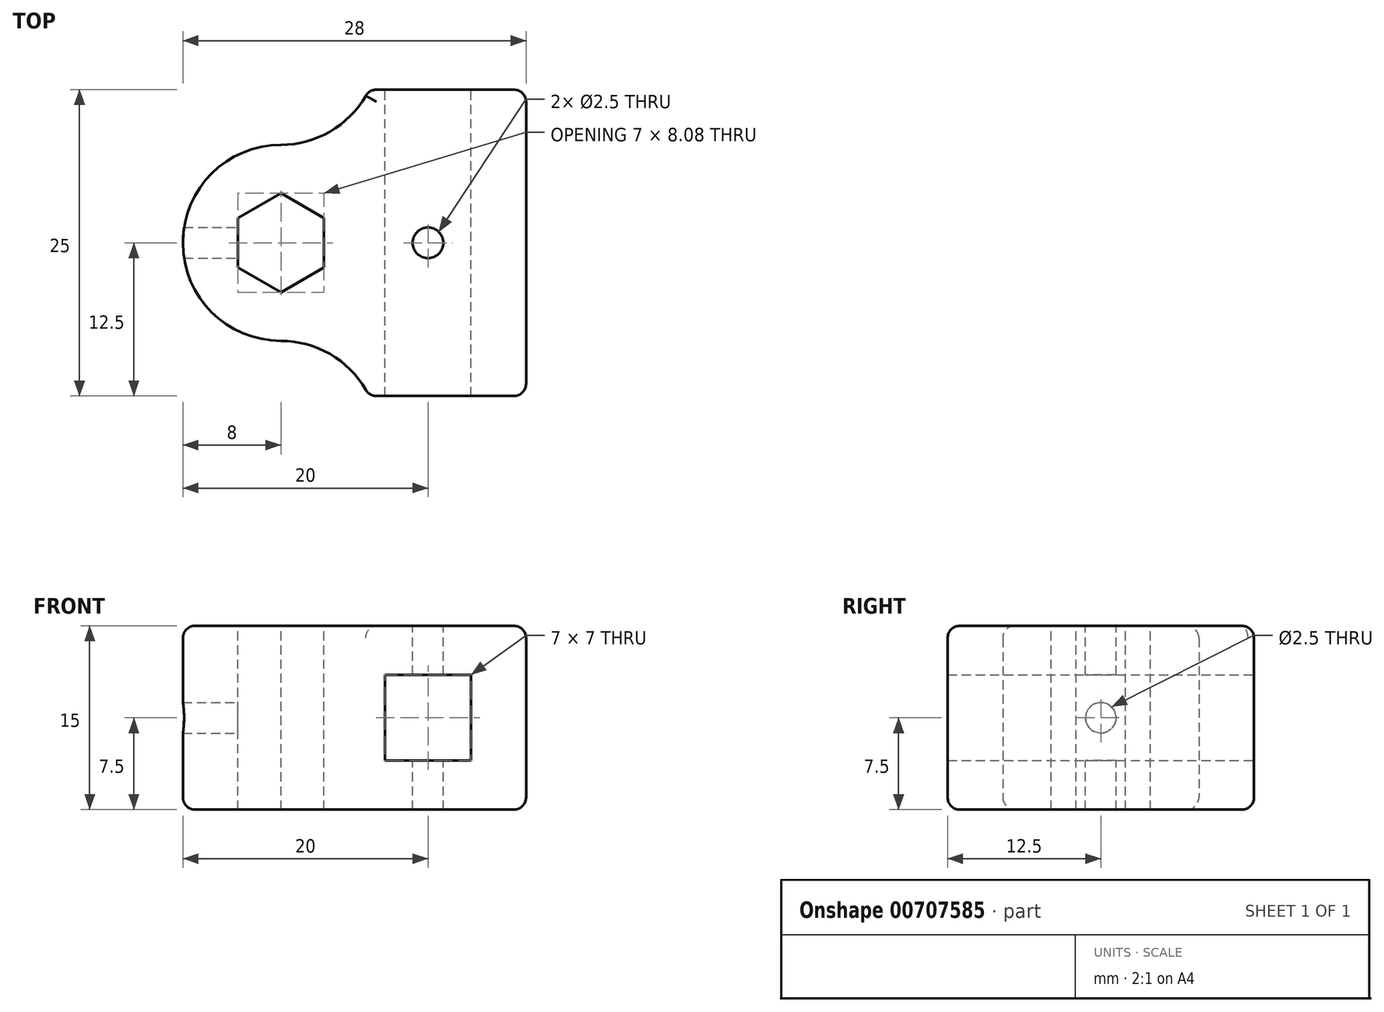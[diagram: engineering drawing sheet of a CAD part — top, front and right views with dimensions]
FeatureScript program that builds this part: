
annotation { "Feature Type Name" : "Feature", "Feature Type Description" : "" }
export const myFeature = defineFeature(function(context is Context, id is Id, definition is map)
    precondition{}
    {
        {
            var Q0;
            Q0=qCreatedBy(makeId("Front.planeOp"),FACE);
            var sketch = newSketch(context, id + "F0", { "sketchPlane" : qUnion([Q0])});
            skLineSegment(sketch, "E0.bottom", {"start": v(-3.5, -3.5) * mm, "end": v(3.5, -3.5) * mm});
            skLineSegment(sketch, "E0.top", {"start": v(-3.5, 3.5) * mm, "end": v(3.5, 3.5) * mm});
            skLineSegment(sketch, "E0.left", {"start": v(-3.5, -3.5) * mm, "end": v(-3.5, 3.5) * mm});
            skLineSegment(sketch, "E0.right", {"start": v(3.5, -3.5) * mm, "end": v(3.5, 3.5) * mm});
            skPoint(sketch, "E0.middle", {"position": v(0, 0) * mm});
            skLineSegment(sketch, "E1.bottom", {"start": v(-20, -7.5) * mm, "end": v(8, -7.5) * mm});
            skLineSegment(sketch, "E1.top", {"start": v(-20, 7.5) * mm, "end": v(8, 7.5) * mm});
            skLineSegment(sketch, "E1.left", {"start": v(-20, -7.5) * mm, "end": v(-20, 7.5) * mm});
            skLineSegment(sketch, "E2", {"start": v(8, 7.5) * mm, "end": v(8, -7.5) * mm});
            skSolve(sketch);
        }
        {
            var Q0;
            Q0=makeQuery(id+"F0.imprint","IMPRINT",FACE,{"disambiguationData":[TD([[makeQuery(id+"F0.imprint","IMPRINT",EDGE,{"derivedFrom":sQuery(id+"F0.wireOp",EDGE,"E0.bottom")}),-1.0]])]});
            extrude(context, id + "F1", {"entities" : qUnion([Q0]), "depth" : 25 * mm, "offsetDistance" : 25 * mm});
        }
        {
            var Q0;
            Q0=qCreatedBy(makeId("Top.planeOp"),FACE);
            var sketch = newSketch(context, id + "F2", { "sketchPlane" : qUnion([Q0])});
            skLineSegment(sketch, "E3", {"start": v(0, 0) * mm, "end": v(0, -12.5) * mm, "construction": true});
            skLineSegment(sketch, "E4", {"start": v(0, -12.5) * mm, "end": v(-35, -12.5) * mm, "construction": true});
            skCircle(sketch, "E5", {"center": v(0, -12.5) * mm, "radius": 1.25 * mm});
            skSolve(sketch);
        }
        {
            var Q0;
            Q0 = qSketchRegion(id + "F2", true);
            extrude(context, id + "F3", {"entities" : qUnion([Q0]), "operationType" : NewBodyOperationType.REMOVE, "oppositeDirection" : true, "depth" : 25 * mm, "offsetDistance" : 25 * mm, "hasSecondDirection" : true, "secondDirectionOppositeDirection" : false, "secondDirectionDepth" : 25 * mm});
        }
        {
            var Q0;
            Q0=qCreatedBy(makeId("Top.planeOp"),FACE);
            var sketch = newSketch(context, id + "F4", { "sketchPlane" : qUnion([Q0])});
            skLineSegment(sketch, "E6", {"start": v(0, 0) * mm, "end": v(-12, 0) * mm, "construction": true});
            skLineSegment(sketch, "E7", {"start": v(-12, 0) * mm, "end": v(-12, -12.5) * mm, "construction": true});
            skLineSegment(sketch, "E8", {"start": v(-12, -12.5) * mm, "end": v(-31.31, -12.5) * mm, "construction": true});
            skCircle(sketch, "E9.cCircle", {"center": v(-12, -12.5) * mm, "radius": 3.5 * mm, "construction": true});
            skLineSegment(sketch, "E9.0", {"start": v(-15.5, -14.52) * mm, "end": v(-15.5, -10.48) * mm});
            skLineSegment(sketch, "E9.1", {"start": v(-15.5, -10.48) * mm, "end": v(-12, -8.46) * mm});
            skLineSegment(sketch, "E9.2", {"start": v(-12, -8.46) * mm, "end": v(-8.5, -10.48) * mm});
            skLineSegment(sketch, "E9.3", {"start": v(-8.5, -10.48) * mm, "end": v(-8.5, -14.52) * mm});
            skLineSegment(sketch, "E9.4", {"start": v(-8.5, -14.52) * mm, "end": v(-12, -16.54) * mm});
            skLineSegment(sketch, "E9.5", {"start": v(-12, -16.54) * mm, "end": v(-15.5, -14.52) * mm});
            skPoint(sketch, "E9.0.midPoint", {"position": v(-15.5, -12.5) * mm});
            skSolve(sketch);
        }
        {
            var Q0;
            Q0 = qSketchRegion(id + "F4", true);
            extrude(context, id + "F5", {"entities" : qUnion([Q0]), "operationType" : NewBodyOperationType.REMOVE, "oppositeDirection" : true, "depth" : 25 * mm, "offsetDistance" : 25 * mm, "hasSecondDirection" : true, "secondDirectionOppositeDirection" : false, "secondDirectionDepth" : 25 * mm});
        }
        {
            var Q0;
            Q0=qCreatedBy(makeId("Right.planeOp"),FACE);
            var sketch = newSketch(context, id + "F6", { "sketchPlane" : qUnion([Q0])});
            skLineSegment(sketch, "E10", {"start": v(0, 0) * mm, "end": v(-12.5, 0) * mm, "construction": true});
            skCircle(sketch, "E11", {"center": v(-12.5, 0) * mm, "radius": 1.25 * mm});
            skSolve(sketch);
        }
        {
            var Q0;
            Q0 = qSketchRegion(id + "F6", true);
            extrude(context, id + "F7", {"entities" : qUnion([Q0]), "operationType" : NewBodyOperationType.REMOVE, "oppositeDirection" : true, "depth" : 25 * mm, "offsetDistance" : 25 * mm, "hasSecondDirection" : true, "secondDirectionOppositeDirection" : true, "secondDirectionDepth" : 10 * mm});
        }
        {
            var Q0;
            Q0=qCreatedBy(makeId("Top.planeOp"),FACE);
            var sketch = newSketch(context, id + "F8", { "sketchPlane" : qUnion([Q0])});
            skLineSegment(sketch, "E12", {"start": v(0, 0) * mm, "end": v(0, -12.5) * mm, "construction": true});
            skLineSegment(sketch, "E13", {"start": v(0, -12.5) * mm, "end": v(-20, -12.5) * mm, "construction": true});
            skLineSegment(sketch, "E14", {"start": v(-20, -12.5) * mm, "end": v(-20, -27.5) * mm, "construction": true});
            skLineSegment(sketch, "E15", {"start": v(-20, -27.5) * mm, "end": v(-12, -27.5) * mm, "construction": true});
            skLineSegment(sketch, "E16", {"start": v(-12, -27.5) * mm, "end": v(-12, -5.5) * mm, "construction": true});
            skArc(sketch, "E17", {"start": v(-20, -12.5) * mm, "mid": v(-17.66, -18.16) * mm, "end": v(-12, -20.5) * mm});
            skLineSegment(sketch, "E18", {"start": v(-12, -12.5) * mm, "end": v(-12, -28.5) * mm, "construction": true});
            skArc(sketch, "E19", {"start": v(-12, -20.5) * mm, "mid": v(-7.24, -22.07) * mm, "end": v(-4.35, -26.17) * mm});
            skLineSegment(sketch, "E20", {"start": v(-4.35, -26.17) * mm, "end": v(8.34, -26.17) * mm});
            skLineSegment(sketch, "E21", {"start": v(8.34, -26.17) * mm, "end": v(8.34, -12.67) * mm});
            skArc(sketch, "E22.MirrorCS", {"start": v(-20, -12.5) * mm, "mid": v(-17.66, -6.84) * mm, "end": v(-12, -4.5) * mm});
            skArc(sketch, "E23.MirrorCS", {"start": v(-12, -4.5) * mm, "mid": v(-7.24, -2.93) * mm, "end": v(-4.35, 1.17) * mm});
            skLineSegment(sketch, "E24.MirrorCS", {"start": v(-4.35, 1.17) * mm, "end": v(8.34, 1.17) * mm});
            skLineSegment(sketch, "E25.MirrorCS", {"start": v(8.34, 1.17) * mm, "end": v(8.34, -12.33) * mm});
            skLineSegment(sketch, "E26", {"start": v(8.34, -12.67) * mm, "end": v(8.34, -12.33) * mm});
            skLineSegment(sketch, "E27.bottom", {"start": v(-21.93, 4.32) * mm, "end": v(21.93, 4.32) * mm});
            skLineSegment(sketch, "E27.top", {"start": v(-21.93, -29.32) * mm, "end": v(21.93, -29.32) * mm});
            skLineSegment(sketch, "E27.left", {"start": v(-21.93, 4.32) * mm, "end": v(-21.93, -29.32) * mm});
            skLineSegment(sketch, "E27.right", {"start": v(21.93, 4.32) * mm, "end": v(21.93, -29.32) * mm});
            skPoint(sketch, "E27.middle", {"position": v(0, -12.5) * mm});
            skSolve(sketch);
        }
        {
            var Q0;
            Q0=makeQuery(id+"F8.imprint","IMPRINT",FACE,{"disambiguationData":[TD([[makeQuery(id+"F8.imprint","IMPRINT",EDGE,{"derivedFrom":sQuery(id+"F8.wireOp",EDGE,"E17")}),-1.0]])]});
            extrude(context, id + "F9", {"entities" : qUnion([Q0]), "operationType" : NewBodyOperationType.REMOVE, "depth" : 25 * mm, "offsetDistance" : 25 * mm, "hasSecondDirection" : true, "secondDirectionOppositeDirection" : true, "secondDirectionDepth" : 25 * mm});
        }
        {
            var Q0;
            Q0=makeQuery(id+"F9.boolean.opBoolean","INTERSECT",EDGE,{"derivedFrom":[makeQuery(id+"F1.opExtrude","SWEPT_FACE",FACE,{"disambiguationData":[OSD([sQuery(id+"F0.wireOp",EDGE,"E1.top")])]}),makeQuery(id+"F9.opExtrude","SWEPT_FACE",FACE,{"disambiguationData":[OSD([sQuery(id+"F8.wireOp",EDGE,"E17"),sQuery(id+"F8.wireOp",EDGE,"E22.MirrorCS")])]})]});
            var Q1;
            Q1=makeQuery(id+"F9.boolean.opBoolean","INTERSECT",EDGE,{"derivedFrom":[makeQuery(id+"F1.opExtrude","SWEPT_FACE",FACE,{"disambiguationData":[OSD([sQuery(id+"F0.wireOp",EDGE,"E1.top")])]}),makeQuery(id+"F9.opExtrude","SWEPT_FACE",FACE,{"disambiguationData":[OSD([sQuery(id+"F8.wireOp",EDGE,"E19")])]})]});
            var Q2;
            Q2=makeQuery(id+"F1.opExtrude","CAP_EDGE",EDGE,{"disambiguationData":[OSD([sQuery(id+"F0.wireOp",EDGE,"E1.top")])],"isStart":false});
            var Q3;
            Q3=makeQuery(id+"F1.opExtrude","SWEPT_EDGE",EDGE,{"disambiguationData":[OSD([sQuery(id+"F0.wireOp",EDGE,"E1.top"),sQuery(id+"F0.wireOp",EDGE,"E2")])]});
            var Q4;
            Q4=makeQuery(id+"F9.boolean.opBoolean","INTERSECT",EDGE,{"derivedFrom":[makeQuery(id+"F1.opExtrude","SWEPT_FACE",FACE,{"disambiguationData":[OSD([sQuery(id+"F0.wireOp",EDGE,"E1.bottom")])]}),makeQuery(id+"F9.opExtrude","SWEPT_FACE",FACE,{"disambiguationData":[OSD([sQuery(id+"F8.wireOp",EDGE,"E19")])]})]});
            var Q5;
            Q5=makeQuery(id+"F9.boolean.opBoolean","INTERSECT",EDGE,{"derivedFrom":[makeQuery(id+"F1.opExtrude","SWEPT_FACE",FACE,{"disambiguationData":[OSD([sQuery(id+"F0.wireOp",EDGE,"E1.bottom")])]}),makeQuery(id+"F9.opExtrude","SWEPT_FACE",FACE,{"disambiguationData":[OSD([sQuery(id+"F8.wireOp",EDGE,"E17"),sQuery(id+"F8.wireOp",EDGE,"E22.MirrorCS")])]})]});
            var Q6;
            Q6=makeQuery(id+"F1.opExtrude","CAP_EDGE",EDGE,{"disambiguationData":[OSD([sQuery(id+"F0.wireOp",EDGE,"E1.bottom")])],"isStart":true});
            var Q7;
            Q7=makeQuery(id+"F1.opExtrude","SWEPT_EDGE",EDGE,{"disambiguationData":[OSD([sQuery(id+"F0.wireOp",EDGE,"E1.bottom"),sQuery(id+"F0.wireOp",EDGE,"E2")])]});
            var Q8;
            Q8=makeQuery(id+"F1.opExtrude","CAP_EDGE",EDGE,{"disambiguationData":[OSD([sQuery(id+"F0.wireOp",EDGE,"E1.bottom")])],"isStart":false});
            fillet(context, id + "F10", {"entities" : qUnion([Q0, Q1, Q2, Q3, Q4, Q5, Q6, Q7, Q8]), "radius" : 1 * mm, "tangentPropagation" : true, "allowEdgeOverflow" : false});
        }
        {
            var Q0;
            Q0=makeQuery(id+"F1.opExtrude","CAP_EDGE",EDGE,{"disambiguationData":[OSD([sQuery(id+"F0.wireOp",EDGE,"E1.top")])],"isStart":true});
            fillet(context, id + "F11", {"entities" : qUnion([Q0]), "radius" : 1 * mm, "tangentPropagation" : true, "allowEdgeOverflow" : false});
        }
        {
            var Q0;
            Q0=makeQuery(id+"F1.opExtrude","CAP_EDGE",EDGE,{"disambiguationData":[OSD([sQuery(id+"F0.wireOp",EDGE,"E2")])],"isStart":false});
            var Q1;
            Q1=makeQuery(id+"F9.boolean.opBoolean","INTERSECT",EDGE,{"derivedFrom":[makeQuery(id+"F1.opExtrude","CAP_FACE",FACE,{"disambiguationData":[OSD([sQuery(id+"F0.wireOp",EDGE,"E0.bottom"),sQuery(id+"F0.wireOp",EDGE,"E0.top"),sQuery(id+"F0.wireOp",EDGE,"E0.left"),sQuery(id+"F0.wireOp",EDGE,"E0.right"),sQuery(id+"F0.wireOp",EDGE,"E1.bottom"),sQuery(id+"F0.wireOp",EDGE,"E1.top"),sQuery(id+"F0.wireOp",EDGE,"E1.left"),sQuery(id+"F0.wireOp",EDGE,"E2")])],"isStart":false}),makeQuery(id+"F9.opExtrude","SWEPT_FACE",FACE,{"disambiguationData":[OSD([sQuery(id+"F8.wireOp",EDGE,"E19")])]})]});
            fillet(context, id + "F12", {"entities" : qUnion([Q0, Q1]), "radius" : 1 * mm, "tangentPropagation" : true, "allowEdgeOverflow" : false});
        }
    });
